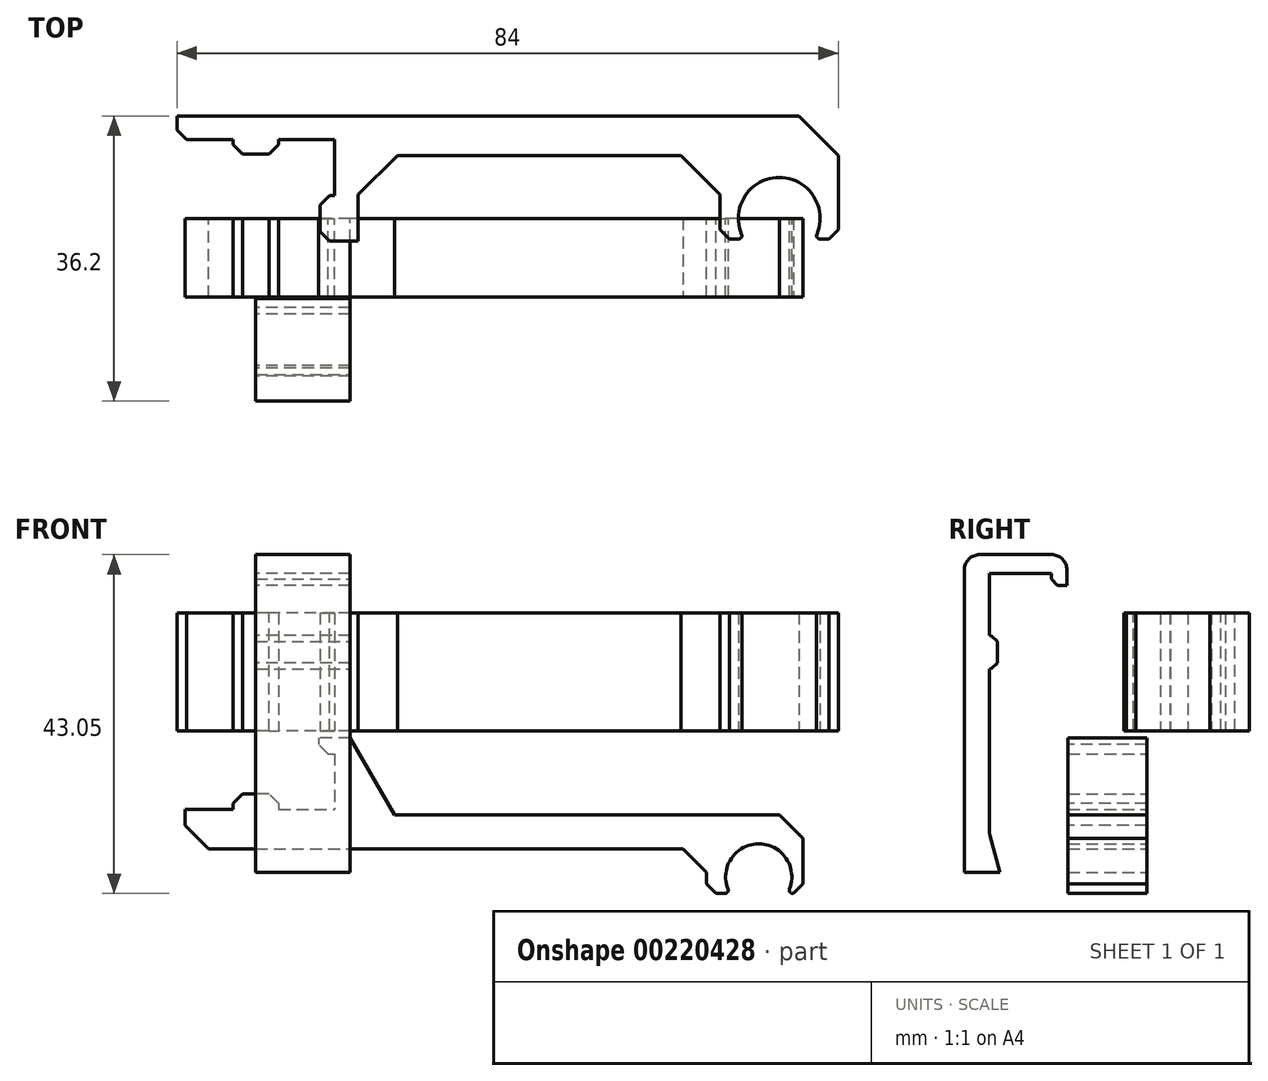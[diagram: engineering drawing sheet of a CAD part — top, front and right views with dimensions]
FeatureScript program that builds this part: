
annotation { "Feature Type Name" : "Feature", "Feature Type Description" : "" }
export const myFeature = defineFeature(function(context is Context, id is Id, definition is map)
    precondition{}
    {
        {
            var Q0;
            Q0=qCreatedBy(makeId("Front.planeOp"),FACE);
            var sketch = newSketch(context, id + "F0", { "sketchPlane" : qUnion([Q0])});
            skLineSegment(sketch, "E0.bottom", {"start": v(9, 10) * mm, "end": v(-9, 10) * mm});
            skLineSegment(sketch, "E0.top", {"start": v(9, -10) * mm, "end": v(-9, -10) * mm});
            skLineSegment(sketch, "E0.left", {"start": v(10, 9) * mm, "end": v(10, -9) * mm});
            skLineSegment(sketch, "E0.right", {"start": v(-10, 9) * mm, "end": v(-10, -9) * mm});
            skPoint(sketch, "E0.middle", {"position": v(0, 0) * mm});
            skPoint(sketch, "E1.visualSharp", {"position": v(10, 10) * mm});
            skArc(sketch, "E1.filletArc", {"start": v(10, 9) * mm, "mid": v(9.7, 9.7) * mm, "end": v(9, 10) * mm});
            skPoint(sketch, "E2.visualSharp", {"position": v(10, -10) * mm});
            skArc(sketch, "E2.filletArc", {"start": v(9, -10) * mm, "mid": v(9.7, -9.7) * mm, "end": v(10, -9) * mm});
            skPoint(sketch, "E3.visualSharp", {"position": v(-10, 10) * mm});
            skArc(sketch, "E3.filletArc", {"start": v(-9, 10) * mm, "mid": v(-9.7, 9.7) * mm, "end": v(-10, 9) * mm});
            skPoint(sketch, "E4.visualSharp", {"position": v(-10, -10) * mm});
            skArc(sketch, "E4.filletArc", {"start": v(-10, -9) * mm, "mid": v(-9.7, -9.7) * mm, "end": v(-9, -10) * mm});
            skLineSegment(sketch, "E5", {"start": v(10, 3) * mm, "end": v(8.2, 3) * mm});
            skLineSegment(sketch, "E6", {"start": v(8.2, 3) * mm, "end": v(8.2, 4.5) * mm});
            skLineSegment(sketch, "E7", {"start": v(8.2, 4.5) * mm, "end": v(5.04, 4.5) * mm});
            skLineSegment(sketch, "E8", {"start": v(10, -3) * mm, "end": v(8.2, -3) * mm});
            skLineSegment(sketch, "E9", {"start": v(8.2, -3) * mm, "end": v(8.2, -4.5) * mm});
            skLineSegment(sketch, "E10", {"start": v(8.2, -4.5) * mm, "end": v(5.04, -4.5) * mm});
            skArc(sketch, "E11", {"start": v(5.04, 4.5) * mm, "mid": v(3.3, 0) * mm, "end": v(5.04, -4.5) * mm});
            skLineSegment(sketch, "E12.1.0", {"start": v(-4.5, 8.2) * mm, "end": v(-4.5, 5.04) * mm});
            skArc(sketch, "E12.1.1", {"start": v(-4.5, 5.04) * mm, "mid": v(0, 3.3) * mm, "end": v(4.5, 5.04) * mm});
            skLineSegment(sketch, "E12.1.2", {"start": v(4.5, 8.2) * mm, "end": v(4.5, 5.04) * mm});
            skLineSegment(sketch, "E12.1.3", {"start": v(3, 8.2) * mm, "end": v(4.5, 8.2) * mm});
            skLineSegment(sketch, "E12.1.4", {"start": v(3, 10) * mm, "end": v(3, 8.2) * mm});
            skLineSegment(sketch, "E12.1.5", {"start": v(-3, 10) * mm, "end": v(-3, 8.2) * mm});
            skLineSegment(sketch, "E12.1.6", {"start": v(-3, 8.2) * mm, "end": v(-4.5, 8.2) * mm});
            skLineSegment(sketch, "E12.2.0", {"start": v(-8.2, -4.5) * mm, "end": v(-5.04, -4.5) * mm});
            skArc(sketch, "E12.2.1", {"start": v(-5.04, -4.5) * mm, "mid": v(-3.3, 0) * mm, "end": v(-5.04, 4.5) * mm});
            skLineSegment(sketch, "E12.2.2", {"start": v(-8.2, 4.5) * mm, "end": v(-5.04, 4.5) * mm});
            skLineSegment(sketch, "E12.2.3", {"start": v(-8.2, 3) * mm, "end": v(-8.2, 4.5) * mm});
            skLineSegment(sketch, "E12.2.4", {"start": v(-10, 3) * mm, "end": v(-8.2, 3) * mm});
            skLineSegment(sketch, "E12.2.5", {"start": v(-10, -3) * mm, "end": v(-8.2, -3) * mm});
            skLineSegment(sketch, "E12.2.6", {"start": v(-8.2, -3) * mm, "end": v(-8.2, -4.5) * mm});
            skLineSegment(sketch, "E12.3.0", {"start": v(4.5, -8.2) * mm, "end": v(4.5, -5.04) * mm});
            skArc(sketch, "E12.3.1", {"start": v(4.5, -5.04) * mm, "mid": v(0, -3.3) * mm, "end": v(-4.5, -5.04) * mm});
            skLineSegment(sketch, "E12.3.2", {"start": v(-4.5, -8.2) * mm, "end": v(-4.5, -5.04) * mm});
            skLineSegment(sketch, "E12.3.3", {"start": v(-3, -8.2) * mm, "end": v(-4.5, -8.2) * mm});
            skLineSegment(sketch, "E12.3.4", {"start": v(-3, -10) * mm, "end": v(-3, -8.2) * mm});
            skLineSegment(sketch, "E12.3.5", {"start": v(3, -10) * mm, "end": v(3, -8.2) * mm});
            skLineSegment(sketch, "E12.3.6", {"start": v(3, -8.2) * mm, "end": v(4.5, -8.2) * mm});
            skSolve(sketch);
        }
        {
            var Q0;
            Q0=qCreatedBy(makeId("Front.planeOp"),FACE);
            var sketch = newSketch(context, id + "F1", { "sketchPlane" : qUnion([Q0])});
            skLineSegment(sketch, "E13.0", {"start": v(10, 9) * mm, "end": v(10, -9) * mm, "construction": true});
            skLineSegment(sketch, "E14.0", {"start": v(9, -10) * mm, "end": v(-9, -10) * mm, "construction": true});
            skLineSegment(sketch, "E15", {"start": v(8, -2.9) * mm, "end": v(10, -2.9) * mm});
            skLineSegment(sketch, "E16", {"start": v(10, -2.9) * mm, "end": v(10, -10) * mm});
            skCircle(sketch, "E17", {"center": v(63.9, -18.55) * mm, "radius": 4.2 * mm});
            skLineSegment(sketch, "E18", {"start": v(-9, -10) * mm, "end": v(-9, -20.65) * mm});
            skLineSegment(sketch, "E19", {"start": v(-9, -20.65) * mm, "end": v(60.26, -20.65) * mm});
            skLineSegment(sketch, "E20", {"start": v(67.54, -20.65) * mm, "end": v(69.54, -20.65) * mm});
            skLineSegment(sketch, "E21", {"start": v(69.54, -20.65) * mm, "end": v(69.54, -10.65) * mm});
            skLineSegment(sketch, "E22", {"start": v(69.54, -10.65) * mm, "end": v(17.63, -10.65) * mm});
            skLineSegment(sketch, "E23", {"start": v(17.63, -10.65) * mm, "end": v(12, -0.9) * mm});
            skLineSegment(sketch, "E24", {"start": v(12, -0.9) * mm, "end": v(8, -0.9) * mm});
            skLineSegment(sketch, "E25", {"start": v(8, -0.9) * mm, "end": v(8, -2.9) * mm});
            skLineSegment(sketch, "E26", {"start": v(-9, -15) * mm, "end": v(57.26, -15) * mm});
            skLineSegment(sketch, "E27", {"start": v(57.26, -15) * mm, "end": v(57.26, -20.65) * mm});
            skLineSegment(sketch, "E28", {"start": v(63.9, -18.55) * mm, "end": v(60.26, -20.65) * mm, "construction": true});
            skLineSegment(sketch, "E29", {"start": v(63.9, -18.55) * mm, "end": v(67.54, -20.65) * mm, "construction": true});
            skLineSegment(sketch, "E30", {"start": v(59.7, -18.55) * mm, "end": v(68.1, -18.55) * mm, "construction": true});
            skLineSegment(sketch, "E31", {"start": v(-9, -10) * mm, "end": v(-2.9, -10) * mm});
            skLineSegment(sketch, "E32", {"start": v(-2.9, -10) * mm, "end": v(-2.9, -8) * mm});
            skLineSegment(sketch, "E33", {"start": v(2.9, -8) * mm, "end": v(-2.9, -8) * mm});
            skLineSegment(sketch, "E34", {"start": v(2.9, -8) * mm, "end": v(2.9, -10) * mm});
            skLineSegment(sketch, "E35", {"start": v(2.9, -10) * mm, "end": v(10, -10) * mm});
            skPoint(sketch, "E36", {"position": v(0, -8) * mm});
            skSolve(sketch);
        }
        {
            var Q0;
            Q0=makeQuery(id+"F1.imprint","IMPRINT",FACE,{"disambiguationData":[TD([[makeQuery(id+"F1.imprint","IMPRINT",EDGE,{"derivedFrom":sQuery(id+"F1.wireOp",EDGE,"E15")}),1.0]])]});
            extrude(context, id + "F2", {"entities" : qUnion([Q0]), "depth" : 10 * mm});
        }
        {
            var Q0;
            Q0=makeQuery(id+"F2.opExtrude","SWEPT_EDGE",EDGE,{"disambiguationData":[OSD([sQuery(id+"F1.wireOp",EDGE,"E32"),sQuery(id+"F1.wireOp",EDGE,"E33")])]});
            var Q1;
            Q1=makeQuery(id+"F2.opExtrude","SWEPT_EDGE",EDGE,{"disambiguationData":[OSD([sQuery(id+"F1.wireOp",EDGE,"E33"),sQuery(id+"F1.wireOp",EDGE,"E34")])]});
            var Q2;
            Q2=makeQuery(id+"F2.opExtrude","SWEPT_EDGE",EDGE,{"disambiguationData":[OSD([sQuery(id+"F1.wireOp",EDGE,"E15"),sQuery(id+"F1.wireOp",EDGE,"E25")])]});
            var Q3;
            Q3=makeQuery(id+"F2.opExtrude","SWEPT_EDGE",EDGE,{"disambiguationData":[OSD([sQuery(id+"F1.wireOp",EDGE,"E19"),sQuery(id+"F1.wireOp",EDGE,"E27")])]});
            var Q4;
            Q4=makeQuery(id+"F2.opExtrude","SWEPT_EDGE",EDGE,{"disambiguationData":[OSD([sQuery(id+"F1.wireOp",EDGE,"E20"),sQuery(id+"F1.wireOp",EDGE,"E21")])]});
            chamfer(context, id + "F3", {"entities" : qUnion([Q0, Q1, Q2, Q3, Q4]), "width" : 1.2 * mm, "tangentPropagation" : true});
        }
        {
            var Q0;
            Q0=makeQuery(id+"F2.opExtrude","SWEPT_EDGE",EDGE,{"disambiguationData":[OSD([sQuery(id+"F1.wireOp",EDGE,"E18"),sQuery(id+"F1.wireOp",EDGE,"E26")])]});
            var Q1;
            Q1=makeQuery(id+"F2.opExtrude","SWEPT_EDGE",EDGE,{"disambiguationData":[OSD([sQuery(id+"F1.wireOp",EDGE,"E26"),sQuery(id+"F1.wireOp",EDGE,"E27")])]});
            var Q2;
            Q2=makeQuery(id+"F2.opExtrude","SWEPT_EDGE",EDGE,{"disambiguationData":[OSD([sQuery(id+"F1.wireOp",EDGE,"E21"),sQuery(id+"F1.wireOp",EDGE,"E22")])]});
            chamfer(context, id + "F4", {"entities" : qUnion([Q0, Q1, Q2]), "width" : 3 * mm, "tangentPropagation" : true});
        }
        {
            var Q0;
            Q0=qCreatedBy(makeId("Top.planeOp"),FACE);
            var sketch = newSketch(context, id + "F5", { "sketchPlane" : qUnion([Q0])});
            skLineSegment(sketch, "E37.bottom", {"start": v(10, 10) * mm, "end": v(-10, 10) * mm, "construction": true});
            skLineSegment(sketch, "E37.top", {"start": v(10, -10) * mm, "end": v(-10, -10) * mm, "construction": true});
            skLineSegment(sketch, "E37.left", {"start": v(10, 10) * mm, "end": v(10, -10) * mm, "construction": true});
            skLineSegment(sketch, "E37.right", {"start": v(-10, 10) * mm, "end": v(-10, -10) * mm, "construction": true});
            skPoint(sketch, "E37.middle", {"position": v(0, 0) * mm});
            skCircle(sketch, "E38", {"center": v(66.5, 0) * mm, "radius": 5.2 * mm});
            skLineSegment(sketch, "E39", {"start": v(-10, 10) * mm, "end": v(-10, 13) * mm});
            skLineSegment(sketch, "E40", {"start": v(-10, 13) * mm, "end": v(74, 13) * mm});
            skLineSegment(sketch, "E41", {"start": v(74, 13) * mm, "end": v(74, -2.6) * mm});
            skLineSegment(sketch, "E42", {"start": v(74, -2.6) * mm, "end": v(71, -2.6) * mm});
            skLineSegment(sketch, "E43", {"start": v(62, -2.6) * mm, "end": v(59, -2.6) * mm});
            skLineSegment(sketch, "E44", {"start": v(59, -2.6) * mm, "end": v(59, 8) * mm});
            skLineSegment(sketch, "E45", {"start": v(59, 8) * mm, "end": v(13, 8) * mm});
            skLineSegment(sketch, "E46", {"start": v(13, 8) * mm, "end": v(13, -2.9) * mm});
            skLineSegment(sketch, "E47", {"start": v(13, -2.9) * mm, "end": v(10, -2.9) * mm});
            skLineSegment(sketch, "E48", {"start": v(10, -2.9) * mm, "end": v(8.2, -2.9) * mm});
            skLineSegment(sketch, "E49", {"start": v(8.2, -2.9) * mm, "end": v(8.2, 2.9) * mm});
            skLineSegment(sketch, "E50", {"start": v(8.2, 2.9) * mm, "end": v(10, 2.9) * mm});
            skLineSegment(sketch, "E51", {"start": v(10, 2.9) * mm, "end": v(10, 10) * mm});
            skLineSegment(sketch, "E52", {"start": v(10, 10) * mm, "end": v(2.9, 10) * mm});
            skLineSegment(sketch, "E53", {"start": v(2.9, 10) * mm, "end": v(2.9, 8.2) * mm});
            skLineSegment(sketch, "E54", {"start": v(2.9, 8.2) * mm, "end": v(-2.9, 8.2) * mm});
            skLineSegment(sketch, "E55", {"start": v(-2.9, 8.2) * mm, "end": v(-2.9, 10) * mm});
            skLineSegment(sketch, "E56", {"start": v(-2.9, 10) * mm, "end": v(-10, 10) * mm});
            skLineSegment(sketch, "E57", {"start": v(61.3, 0) * mm, "end": v(71.7, 0) * mm, "construction": true});
            skLineSegment(sketch, "E58", {"start": v(66.5, 0) * mm, "end": v(62, -2.6) * mm, "construction": true});
            skLineSegment(sketch, "E59", {"start": v(66.5, 0) * mm, "end": v(71, -2.6) * mm, "construction": true});
            skPoint(sketch, "E60", {"position": v(0, 8.2) * mm});
            skPoint(sketch, "E61", {"position": v(8.2, 0) * mm});
            skSolve(sketch);
        }
        {
            var Q0;
            Q0=makeQuery(id+"F5.imprint","IMPRINT",FACE,{"disambiguationData":[TD([[makeQuery(id+"F5.imprint","IMPRINT",EDGE,{"derivedFrom":sQuery(id+"F5.wireOp",EDGE,"E39")}),-1.0]])]});
            extrude(context, id + "F6", {"entities" : qUnion([Q0]), "depth" : 15 * mm});
        }
        {
            var Q0;
            Q0=makeQuery(id+"F6.opExtrude","SWEPT_EDGE",EDGE,{"disambiguationData":[OSD([sQuery(id+"F5.wireOp",EDGE,"E49"),sQuery(id+"F5.wireOp",EDGE,"E50")])]});
            var Q1;
            Q1=makeQuery(id+"F6.opExtrude","SWEPT_EDGE",EDGE,{"disambiguationData":[OSD([sQuery(id+"F5.wireOp",EDGE,"E48"),sQuery(id+"F5.wireOp",EDGE,"E49")])]});
            var Q2;
            Q2=makeQuery(id+"F6.opExtrude","SWEPT_EDGE",EDGE,{"disambiguationData":[OSD([sQuery(id+"F5.wireOp",EDGE,"E54"),sQuery(id+"F5.wireOp",EDGE,"E55")])]});
            var Q3;
            Q3=makeQuery(id+"F6.opExtrude","SWEPT_EDGE",EDGE,{"disambiguationData":[OSD([sQuery(id+"F5.wireOp",EDGE,"E53"),sQuery(id+"F5.wireOp",EDGE,"E54")])]});
            var Q4;
            Q4=makeQuery(id+"F6.opExtrude","SWEPT_EDGE",EDGE,{"disambiguationData":[OSD([sQuery(id+"F5.wireOp",EDGE,"E39"),sQuery(id+"F5.wireOp",EDGE,"E56")])]});
            var Q5;
            Q5=makeQuery(id+"F6.opExtrude","SWEPT_EDGE",EDGE,{"disambiguationData":[OSD([sQuery(id+"F5.wireOp",EDGE,"E43"),sQuery(id+"F5.wireOp",EDGE,"E44")])]});
            var Q6;
            Q6=makeQuery(id+"F6.opExtrude","SWEPT_EDGE",EDGE,{"disambiguationData":[OSD([sQuery(id+"F5.wireOp",EDGE,"E41"),sQuery(id+"F5.wireOp",EDGE,"E42")])]});
            chamfer(context, id + "F7", {"entities" : qUnion([Q0, Q1, Q2, Q3, Q4, Q5, Q6]), "width" : 1.2 * mm, "tangentPropagation" : true});
        }
        {
            var Q0;
            Q0=makeQuery(id+"F6.opExtrude","SWEPT_EDGE",EDGE,{"disambiguationData":[OSD([sQuery(id+"F5.wireOp",EDGE,"E40"),sQuery(id+"F5.wireOp",EDGE,"E41")])]});
            var Q1;
            Q1=makeQuery(id+"F6.opExtrude","SWEPT_EDGE",EDGE,{"disambiguationData":[OSD([sQuery(id+"F5.wireOp",EDGE,"E44"),sQuery(id+"F5.wireOp",EDGE,"E45")])]});
            var Q2;
            Q2=makeQuery(id+"F6.opExtrude","SWEPT_EDGE",EDGE,{"disambiguationData":[OSD([sQuery(id+"F5.wireOp",EDGE,"E45"),sQuery(id+"F5.wireOp",EDGE,"E46")])]});
            chamfer(context, id + "F8", {"entities" : qUnion([Q0, Q1, Q2]), "width" : 5 * mm, "tangentPropagation" : true});
        }
        {
            var Q0;
            Q0=makeQuery(id+"F2.opExtrude","SWEPT_EDGE",EDGE,{"disambiguationData":[OSD([sQuery(id+"F1.wireOp",EDGE,"E17"),sQuery(id+"F1.wireOp",EDGE,"E19")])]});
            var Q1;
            Q1=makeQuery(id+"F2.opExtrude","SWEPT_EDGE",EDGE,{"disambiguationData":[OSD([sQuery(id+"F1.wireOp",EDGE,"E17"),sQuery(id+"F1.wireOp",EDGE,"E20")])]});
            var Q2;
            Q2=makeQuery(id+"F6.opExtrude","SWEPT_EDGE",EDGE,{"disambiguationData":[OSD([sQuery(id+"F5.wireOp",EDGE,"E38"),sQuery(id+"F5.wireOp",EDGE,"E43")])]});
            var Q3;
            Q3=makeQuery(id+"F6.opExtrude","SWEPT_EDGE",EDGE,{"disambiguationData":[OSD([sQuery(id+"F5.wireOp",EDGE,"E38"),sQuery(id+"F5.wireOp",EDGE,"E42")])]});
            fillet(context, id + "F9", {"entities" : qUnion([Q0, Q1, Q2, Q3]), "radius" : 0.4 * mm, "tangentPropagation" : true, "allowEdgeOverflow" : false});
        }
        {
            var Q0;
            Q0=qCreatedBy(makeId("Right.planeOp"),FACE);
            var sketch = newSketch(context, id + "F10", { "sketchPlane" : qUnion([Q0])});
            skLineSegment(sketch, "E62.bottom", {"start": v(0, 0) * mm, "end": v(-20, 0) * mm, "construction": true});
            skLineSegment(sketch, "E62.top", {"start": v(0, 20) * mm, "end": v(-20, 20) * mm, "construction": true});
            skLineSegment(sketch, "E62.left", {"start": v(0, 0) * mm, "end": v(0, 20) * mm, "construction": true});
            skLineSegment(sketch, "E62.right", {"start": v(-20, 0) * mm, "end": v(-20, 20) * mm, "construction": true});
            skLineSegment(sketch, "E63", {"start": v(-12.15, 18.5) * mm, "end": v(-12.15, 20) * mm});
            skLineSegment(sketch, "E64", {"start": v(-12.15, 20) * mm, "end": v(-20, 20) * mm});
            skLineSegment(sketch, "E65", {"start": v(-20, 12.15) * mm, "end": v(-19, 12.15) * mm});
            skLineSegment(sketch, "E66", {"start": v(-19, 12.15) * mm, "end": v(-19, 7.85) * mm});
            skLineSegment(sketch, "E67", {"start": v(-19, 7.85) * mm, "end": v(-20, 7.85) * mm});
            skLineSegment(sketch, "E68", {"start": v(-20, 7.85) * mm, "end": v(-20, -13) * mm});
            skLineSegment(sketch, "E69", {"start": v(-18.66, -18) * mm, "end": v(-23.2, -18) * mm});
            skLineSegment(sketch, "E70", {"start": v(-23.2, -18) * mm, "end": v(-23.2, 22.4) * mm});
            skLineSegment(sketch, "E71", {"start": v(-23.2, 22.4) * mm, "end": v(-10.15, 22.4) * mm});
            skLineSegment(sketch, "E72", {"start": v(-10.15, 22.4) * mm, "end": v(-10.15, 18.5) * mm});
            skLineSegment(sketch, "E73", {"start": v(-10.15, 18.5) * mm, "end": v(-12.15, 18.5) * mm});
            skLineSegment(sketch, "E74", {"start": v(-20, -13) * mm, "end": v(-18.66, -18) * mm});
            skLineSegment(sketch, "E75", {"start": v(-20, 20) * mm, "end": v(-20, 12.15) * mm});
            skSolve(sketch);
        }
        {
            var Q0;
            Q0=makeQuery(id+"F10.imprint","IMPRINT",FACE,{"disambiguationData":[TD([[makeQuery(id+"F10.imprint","IMPRINT",EDGE,{"derivedFrom":sQuery(id+"F10.wireOp",EDGE,"E63")}),-1.0]])]});
            extrude(context, id + "F11", {"entities" : qUnion([Q0]), "depth" : 12 * mm});
        }
        {
            var Q0;
            Q0=makeQuery(id+"F11.opExtrude","SWEPT_EDGE",EDGE,{"disambiguationData":[OSD([sQuery(id+"F10.wireOp",EDGE,"E65"),sQuery(id+"F10.wireOp",EDGE,"E66")])]});
            var Q1;
            Q1=makeQuery(id+"F11.opExtrude","SWEPT_EDGE",EDGE,{"disambiguationData":[OSD([sQuery(id+"F10.wireOp",EDGE,"E63"),sQuery(id+"F10.wireOp",EDGE,"E73")])]});
            var Q2;
            Q2=makeQuery(id+"F11.opExtrude","SWEPT_EDGE",EDGE,{"disambiguationData":[OSD([sQuery(id+"F10.wireOp",EDGE,"E66"),sQuery(id+"F10.wireOp",EDGE,"E67")])]});
            chamfer(context, id + "F12", {"entities" : qUnion([Q0, Q1, Q2]), "width" : 0.8 * mm, "tangentPropagation" : true});
        }
        {
            var Q0;
            Q0=makeQuery(id+"F11.opExtrude","SWEPT_EDGE",EDGE,{"disambiguationData":[OSD([sQuery(id+"F10.wireOp",EDGE,"E70"),sQuery(id+"F10.wireOp",EDGE,"E71")])]});
            var Q1;
            Q1=makeQuery(id+"F11.opExtrude","SWEPT_EDGE",EDGE,{"disambiguationData":[OSD([sQuery(id+"F10.wireOp",EDGE,"E68"),sQuery(id+"F10.wireOp",EDGE,"E74")])]});
            var Q2;
            Q2=makeQuery(id+"F11.opExtrude","SWEPT_EDGE",EDGE,{"disambiguationData":[OSD([sQuery(id+"F10.wireOp",EDGE,"E71"),sQuery(id+"F10.wireOp",EDGE,"E72")])]});
            fillet(context, id + "F13", {"entities" : qUnion([Q0, Q1, Q2]), "radius" : 2 * mm, "tangentPropagation" : true, "allowEdgeOverflow" : false});
        }
    });
